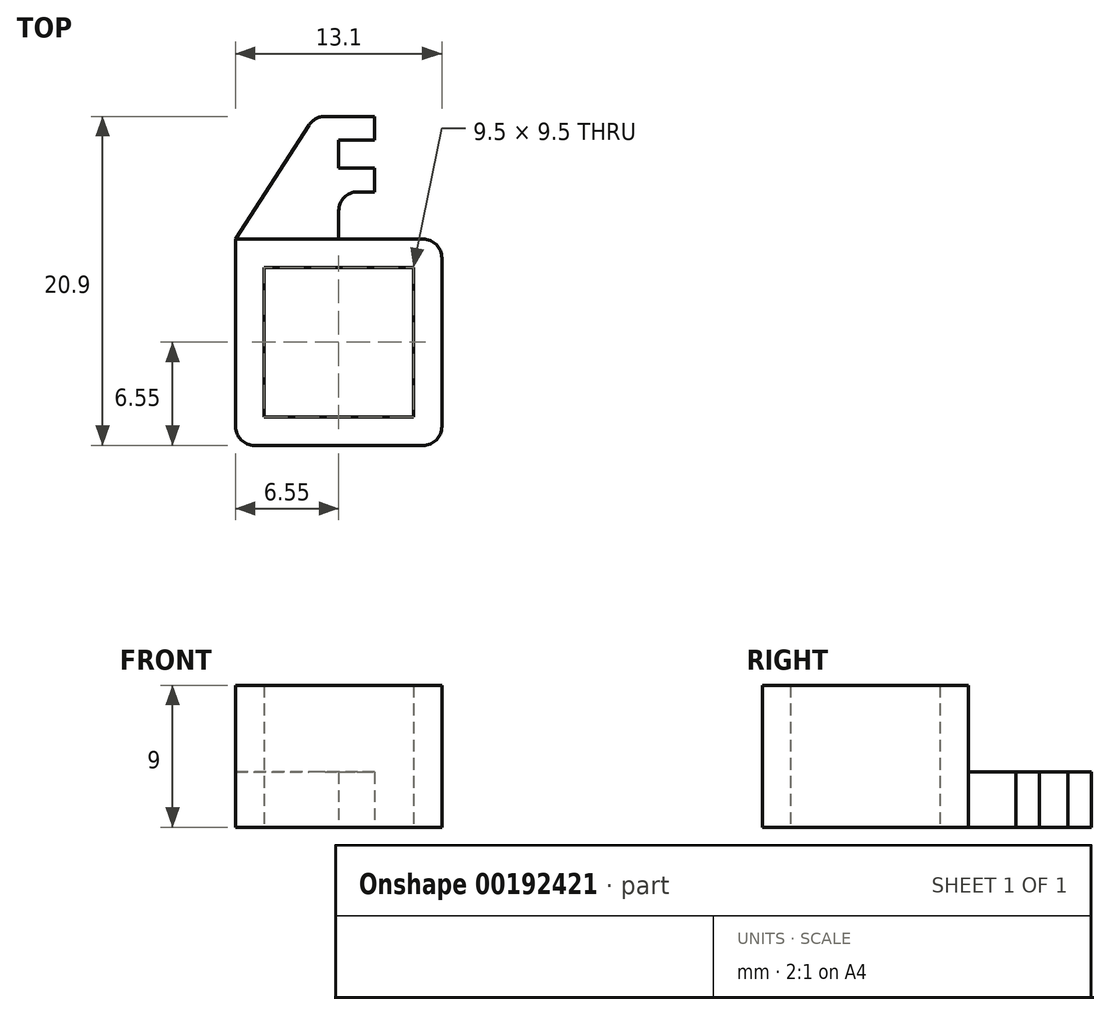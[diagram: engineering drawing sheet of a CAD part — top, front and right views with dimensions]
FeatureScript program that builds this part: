
annotation { "Feature Type Name" : "Feature", "Feature Type Description" : "" }
export const myFeature = defineFeature(function(context is Context, id is Id, definition is map)
    precondition{}
    {
        {
            var Q0;
            Q0=qCreatedBy(makeId("Top.planeOp"),FACE);
            var sketch = newSketch(context, id + "F0", { "sketchPlane" : qUnion([Q0])});
            skLineSegment(sketch, "E0.bottom", {"start": v(4.75, -4.75) * mm, "end": v(-4.75, -4.75) * mm});
            skLineSegment(sketch, "E0.top", {"start": v(4.75, 4.75) * mm, "end": v(-4.75, 4.75) * mm});
            skLineSegment(sketch, "E0.left", {"start": v(4.75, -4.75) * mm, "end": v(4.75, 4.75) * mm});
            skLineSegment(sketch, "E0.right", {"start": v(-4.75, -4.75) * mm, "end": v(-4.75, 4.75) * mm});
            skPoint(sketch, "E0.middle", {"position": v(0, 0) * mm});
            skLineSegment(sketch, "E1.0", {"start": v(6.55, 6.55) * mm, "end": v(-6.55, 6.55) * mm});
            skLineSegment(sketch, "E1.1", {"start": v(6.55, -6.55) * mm, "end": v(6.55, 6.55) * mm});
            skLineSegment(sketch, "E1.2", {"start": v(6.55, -6.55) * mm, "end": v(-6.55, -6.55) * mm});
            skLineSegment(sketch, "E1.3", {"start": v(-6.55, -6.55) * mm, "end": v(-6.55, 6.55) * mm});
            skLineSegment(sketch, "E2", {"start": v(-6.55, 6.55) * mm, "end": v(-1.53, 14.35) * mm});
            skLineSegment(sketch, "E3", {"start": v(-1.53, 14.35) * mm, "end": v(2.27, 14.35) * mm});
            skLineSegment(sketch, "E4", {"start": v(2.27, 14.35) * mm, "end": v(2.27, 12.85) * mm});
            skLineSegment(sketch, "E5", {"start": v(2.27, 12.85) * mm, "end": v(0, 12.85) * mm});
            skLineSegment(sketch, "E6", {"start": v(0, 12.85) * mm, "end": v(0, 11.05) * mm});
            skLineSegment(sketch, "E7", {"start": v(0, 11.05) * mm, "end": v(2.27, 11.05) * mm});
            skLineSegment(sketch, "E8", {"start": v(2.27, 11.05) * mm, "end": v(2.27, 9.55) * mm});
            skLineSegment(sketch, "E9", {"start": v(2.27, 9.55) * mm, "end": v(0, 9.55) * mm});
            skLineSegment(sketch, "E10", {"start": v(0, 9.55) * mm, "end": v(0, 6.55) * mm});
            skSolve(sketch);
        }
        {
            var Q0;
            Q0=makeQuery(id+"F0.imprint","IMPRINT",FACE,{"disambiguationData":[TD([[makeQuery(id+"F0.imprint","IMPRINT",EDGE,{"derivedFrom":sQuery(id+"F0.wireOp",EDGE,"E0.bottom")}),1.0]])]});
            extrude(context, id + "F1", {"entities" : qUnion([Q0]), "depth" : 9 * mm});
        }
        {
            var Q0;
            Q0=makeQuery(id+"F1.opExtrude","SWEPT_EDGE",EDGE,{"disambiguationData":[OSD([sQuery(id+"F0.wireOp",EDGE,"E1.0"),sQuery(id+"F0.wireOp",EDGE,"E1.1")])]});
            var Q1;
            Q1=makeQuery(id+"F1.opExtrude","SWEPT_EDGE",EDGE,{"disambiguationData":[OSD([sQuery(id+"F0.wireOp",EDGE,"E1.1"),sQuery(id+"F0.wireOp",EDGE,"E1.2")])]});
            var Q2;
            Q2=makeQuery(id+"F1.opExtrude","SWEPT_EDGE",EDGE,{"disambiguationData":[OSD([sQuery(id+"F0.wireOp",EDGE,"E1.2"),sQuery(id+"F0.wireOp",EDGE,"E1.3")])]});
            fillet(context, id + "F2", {"entities" : qUnion([Q0, Q1, Q2]), "radius" : 1.2 * mm, "tangentPropagation" : true, "allowEdgeOverflow" : false});
        }
        {
            var Q0;
            {var subQ0=sQuery(id+"F0.wireOp",EDGE,"E2");Q0=makeQuery(id+"F0.imprint","IMPRINT",FACE,{"disambiguationData":[TD([[makeQuery(id+"F0.imprint","IMPRINT",EDGE,{"derivedFrom":subQ0}),-1.0]])]});}
            extrude(context, id + "F3", {"entities" : qUnion([Q0]), "operationType" : NewBodyOperationType.ADD, "depth" : 3.5 * mm});
        }
        {
            var Q0;
            Q0=makeQuery(id+"F3.opExtrude","SWEPT_EDGE",EDGE,{"disambiguationData":[OSD([sQuery(id+"F0.wireOp",EDGE,"E1.0"),sQuery(id+"F0.wireOp",EDGE,"E10")])]});
            var Q1;
            Q1=makeQuery(id+"F3.opExtrude","CAP_EDGE",EDGE,{"disambiguationData":[OSD([sQuery(id+"F0.wireOp",EDGE,"E1.0")])],"isStart":false});
            var Q2;
            Q2=makeQuery(id+"F3.opExtrude","SWEPT_EDGE",EDGE,{"disambiguationData":[OSD([sQuery(id+"F0.wireOp",EDGE,"E2"),sQuery(id+"F0.wireOp",EDGE,"E3")])]});
            var Q3;
            Q3=makeQuery(id+"F3.opExtrude","SWEPT_EDGE",EDGE,{"disambiguationData":[OSD([sQuery(id+"F0.wireOp",EDGE,"E9"),sQuery(id+"F0.wireOp",EDGE,"E10")])]});
            fillet(context, id + "F4", {"entities" : qUnion([Q0, Q1, Q2, Q3]), "radius" : 1.2 * mm, "tangentPropagation" : true, "allowEdgeOverflow" : false});
        }
    });
